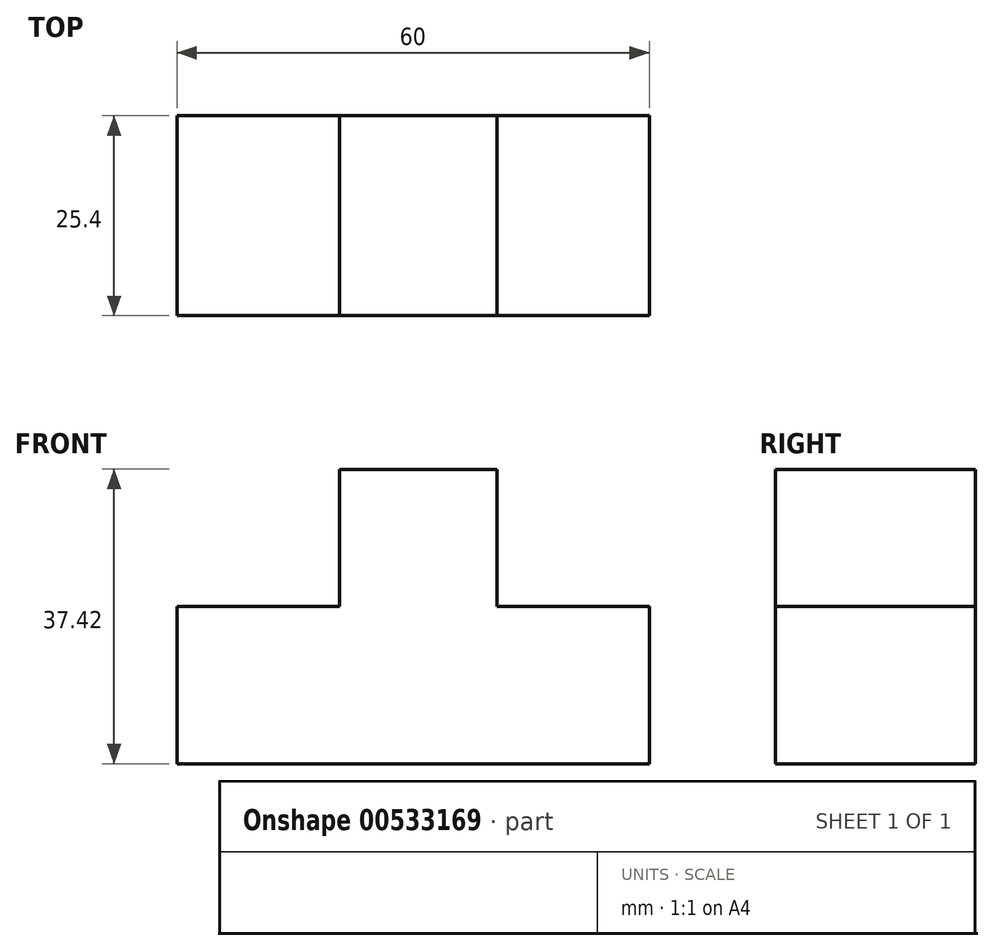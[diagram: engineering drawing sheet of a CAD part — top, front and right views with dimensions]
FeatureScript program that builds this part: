
annotation { "Feature Type Name" : "Feature", "Feature Type Description" : "" }
export const myFeature = defineFeature(function(context is Context, id is Id, definition is map)
    precondition{}
    {
        {
            var Q0;
            Q0=qCreatedBy(makeId("Front.planeOp"),FACE);
            var sketch = newSketch(context, id + "F0", { "sketchPlane" : qUnion([Q0])});
            skLineSegment(sketch, "E0.bottom", {"start": v(-24.92, 30.4) * mm, "end": v(-4.92, 30.4) * mm});
            skLineSegment(sketch, "E0.top", {"start": v(-24.92, 12.88) * mm, "end": v(-4.92, 12.88) * mm});
            skLineSegment(sketch, "E0.left", {"start": v(-24.92, 30.4) * mm, "end": v(-24.92, 12.88) * mm});
            skLineSegment(sketch, "E0.right", {"start": v(-4.92, 30.4) * mm, "end": v(-4.92, 12.88) * mm});
            skLineSegment(sketch, "E1.bottom", {"start": v(-45.57, 12.99) * mm, "end": v(14.43, 12.99) * mm});
            skLineSegment(sketch, "E1.top", {"start": v(-45.57, -7.01) * mm, "end": v(14.43, -7.01) * mm});
            skLineSegment(sketch, "E1.left", {"start": v(-45.57, 12.99) * mm, "end": v(-45.57, -7.01) * mm});
            skLineSegment(sketch, "E1.right", {"start": v(14.43, 12.99) * mm, "end": v(14.43, -7.01) * mm});
            skSolve(sketch);
        }
        {
            var Q0;
            Q0 = qSketchRegion(id + "F0", true);
            extrude(context, id + "F1", {"entities" : qUnion([Q0]), "depth" : 25.4 * mm, "offsetDistance" : 25.4 * mm});
        }
    });
